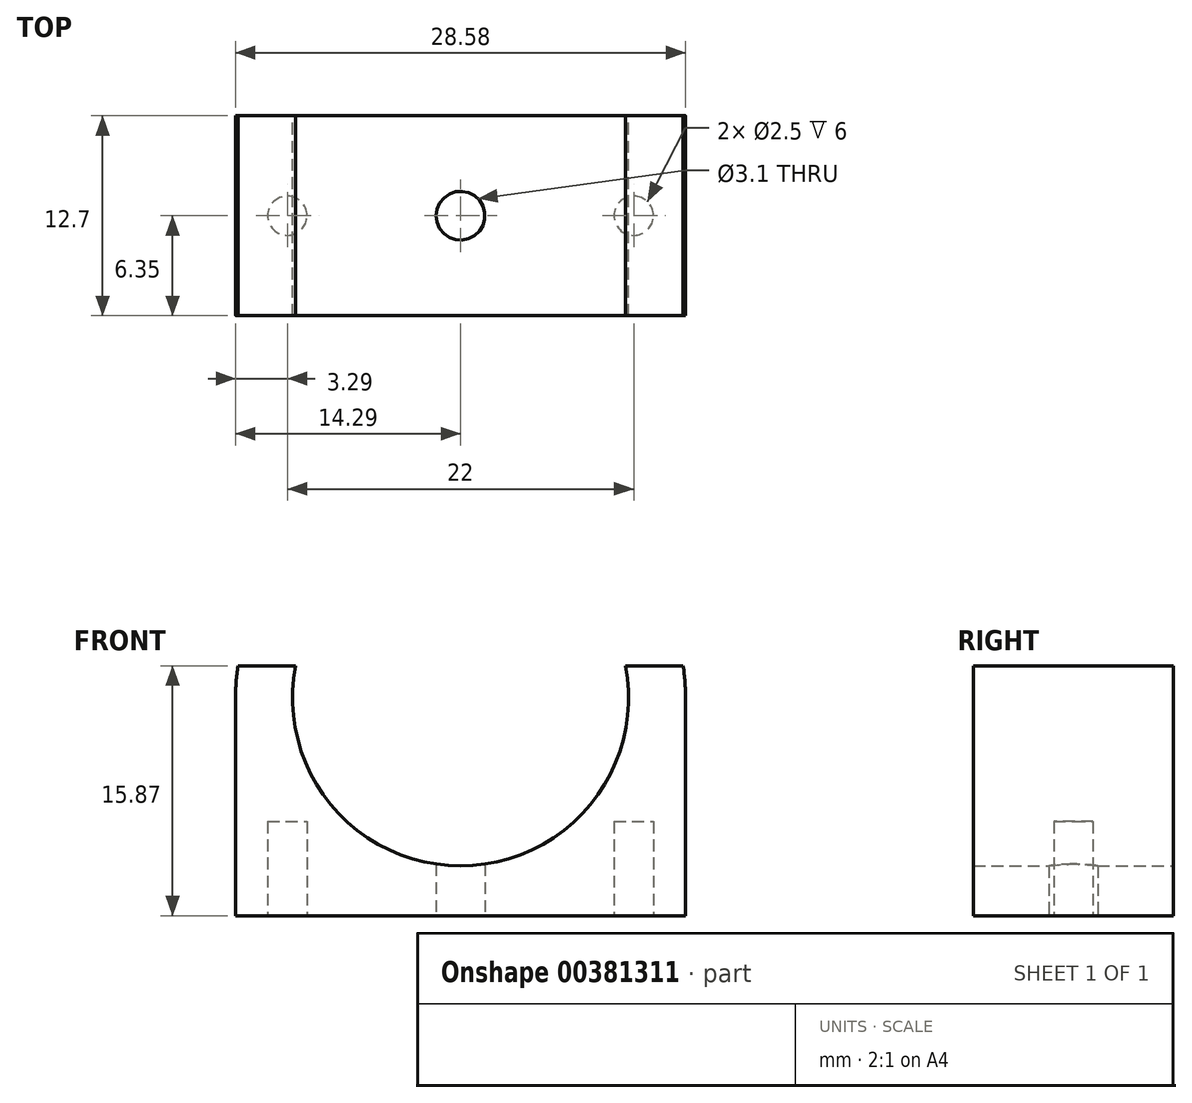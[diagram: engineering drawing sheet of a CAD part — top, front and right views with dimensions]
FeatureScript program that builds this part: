
annotation { "Feature Type Name" : "Feature", "Feature Type Description" : "" }
export const myFeature = defineFeature(function(context is Context, id is Id, definition is map)
    precondition{}
    {
        {
            var Q0;
            Q0=qCreatedBy(makeId("Front.planeOp"),FACE);
            var sketch = newSketch(context, id + "F0", { "sketchPlane" : qUnion([Q0])});
            skArc(sketch, "E0", {"start": v(-10.47, 2.03) * mm, "mid": v(0, -10.67) * mm, "end": v(10.47, 2.03) * mm});
            skLineSegment(sketch, "E1", {"start": v(-14.29, 0) * mm, "end": v(-14.29, -13.84) * mm});
            skLineSegment(sketch, "E2", {"start": v(-14.29, -13.84) * mm, "end": v(14.29, -13.84) * mm});
            skLineSegment(sketch, "E3", {"start": v(14.29, -13.84) * mm, "end": v(14.29, 0) * mm});
            skLineSegment(sketch, "E4", {"start": v(-14.14, 2.03) * mm, "end": v(-10.47, 2.03) * mm});
            skLineSegment(sketch, "E5.trimOffspring", {"start": v(10.47, 2.03) * mm, "end": v(14.14, 2.03) * mm});
            skArc(sketch, "E6", {"start": v(14.29, 0) * mm, "mid": v(14.25, 1.02) * mm, "end": v(14.14, 2.03) * mm});
            skArc(sketch, "E7.trimOffspring", {"start": v(-14.14, 2.03) * mm, "mid": v(-14.25, 1.02) * mm, "end": v(-14.29, 0) * mm});
            skSolve(sketch);
        }
        {
            var Q0;
            Q0=makeQuery(id+"F0.imprint","IMPRINT",FACE,{"disambiguationData":[TD([[makeQuery(id+"F0.imprint","IMPRINT",EDGE,{"derivedFrom":sQuery(id+"F0.wireOp",EDGE,"E0")}),-1.0]])]});
            extrude(context, id + "F1", {"entities" : qUnion([Q0]), "depth" : 12.7 * mm});
        }
        {
            var Q0;
            Q0=makeQuery(id+"F1.opExtrude","SWEPT_FACE",FACE,{"disambiguationData":[OSD([sQuery(id+"F0.wireOp",EDGE,"E2")])]});
            var sketch = newSketch(context, id + "F2", { "sketchPlane" : qUnion([Q0])});
            skCircle(sketch, "E8", {"center": v(-11, 6.35) * mm, "radius": 1.25 * mm});
            skCircle(sketch, "E9", {"center": v(11, 6.35) * mm, "radius": 1.25 * mm});
            skCircle(sketch, "E10", {"center": v(0, 6.35) * mm, "radius": 1.55 * mm});
            skSolve(sketch);
        }
        {
            var Q0;
            Q0 = qSketchRegion(id + "F2", true);
            extrude(context, id + "F3", {"entities" : qUnion([Q0]), "operationType" : NewBodyOperationType.REMOVE, "oppositeDirection" : true, "depth" : 6 * mm});
        }
    });
